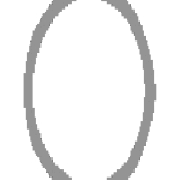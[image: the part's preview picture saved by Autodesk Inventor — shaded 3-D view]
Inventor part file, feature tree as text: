
AUTODESK INVENTOR PART (.ipt)
format: ipt  version: 2021 (Build 250183000, 183)  size: 109,568 bytes
history: native  units: in
note: dims shown in document units (in); Inventor stores cm internally (conversion verified against a paired STEP export)
features: other x4, sketch x3, plane x1
ambient origin geometry x8: Origin, YZ Plane, XZ Plane, XY Plane, X Axis, Y Axis, Z Axis, Center Point
bodies: Solid1 (feature_tree), Body (feature_tree)
feature tree (8):
  other  "Driven Length"
  other  "Frame Generator"
  other  "Start Plane"
  other  "End Plane"
  sketch  "Sketch"  dims[d2=20.6216in d4=-0.0in d5=20.6216in d6=0.12in d7=0.0in d8=90.0deg d9=20.6216in]
  sketch  "Sketch2"  dims[d0=1.0in]
  plane  "Work Plane3"
  sketch  "Sketch3"  dims[d1=0.065in]
